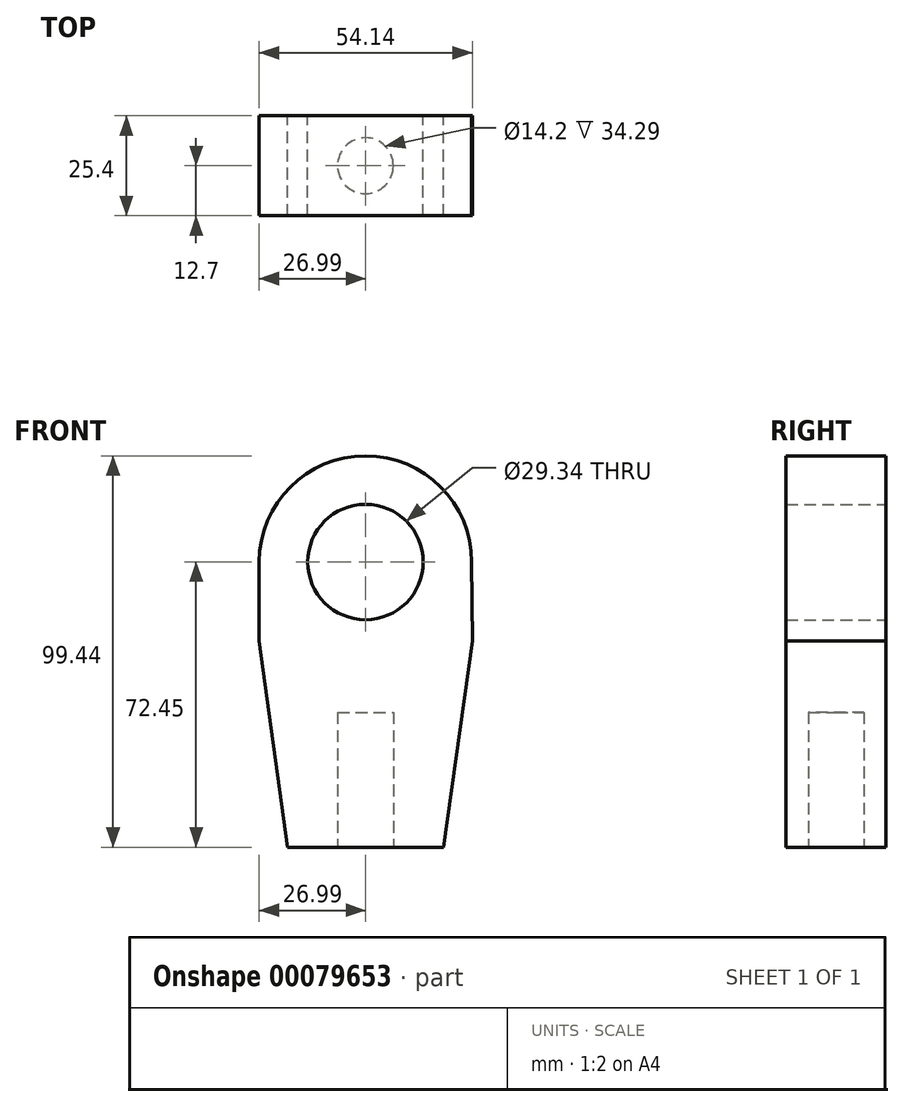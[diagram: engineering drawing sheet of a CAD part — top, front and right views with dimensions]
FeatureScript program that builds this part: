
annotation { "Feature Type Name" : "Feature", "Feature Type Description" : "" }
export const myFeature = defineFeature(function(context is Context, id is Id, definition is map)
    precondition{}
    {
        {
            var Q0;
            Q0=qCreatedBy(makeId("Front.planeOp"),FACE);
            var sketch = newSketch(context, id + "F0", { "sketchPlane" : qUnion([Q0])});
            skCircle(sketch, "E0", {"center": v(0, 0) * mm, "radius": 14.67 * mm});
            skCircle(sketch, "E1", {"center": v(0, 0) * mm, "radius": 26.99 * mm, "construction": true});
            skLineSegment(sketch, "E2", {"start": v(0, 26.99) * mm, "end": v(0, -72.45) * mm, "construction": true});
            skLineSegment(sketch, "E3", {"start": v(0, -72.45) * mm, "end": v(-19.81, -72.45) * mm});
            skLineSegment(sketch, "E4", {"start": v(0, -72.45) * mm, "end": v(19.81, -72.45) * mm});
            skArc(sketch, "E5", {"start": v(26.99, 0) * mm, "mid": v(0, 26.99) * mm, "end": v(-26.99, 0) * mm});
            skLineSegment(sketch, "E6", {"start": v(0, 26.99) * mm, "end": v(0, -20) * mm, "construction": true});
            skLineSegment(sketch, "E7", {"start": v(0, -20) * mm, "end": v(-28.93, -20) * mm, "construction": true});
            skLineSegment(sketch, "E8", {"start": v(0, -20) * mm, "end": v(27.15, -20) * mm, "construction": true});
            skLineSegment(sketch, "E9", {"start": v(-26.99, 0) * mm, "end": v(-26.99, -20) * mm});
            skLineSegment(sketch, "E10", {"start": v(26.99, 0) * mm, "end": v(27.15, -20) * mm});
            skLineSegment(sketch, "E11", {"start": v(-26.99, -20) * mm, "end": v(-19.81, -72.45) * mm});
            skLineSegment(sketch, "E12", {"start": v(27.15, -20) * mm, "end": v(19.81, -72.45) * mm});
            skSolve(sketch);
        }
        {
            var Q0;
            Q0 = qSketchRegion(id + "F0", true);
            extrude(context, id + "F1", {"entities" : qUnion([Q0]), "depth" : 25.4 * mm});
        }
        {
            var Q0;
            Q0=makeQuery(id+"F1.opExtrude","SWEPT_FACE",FACE,{"disambiguationData":[OSD([sQuery(id+"F0.wireOp",EDGE,"E3"),sQuery(id+"F0.wireOp",EDGE,"E4")])]});
            var sketch = newSketch(context, id + "F2", { "sketchPlane" : qUnion([Q0])});
            skCircle(sketch, "E13", {"center": v(0, 12.7) * mm, "radius": 7.1 * mm});
            skSolve(sketch);
        }
        {
            var Q0;
            Q0=makeQuery(id+"F2.imprint","IMPRINT",FACE,{"disambiguationData":[TD([[makeQuery(id+"F2.imprint","IMPRINT",EDGE,{"derivedFrom":sQuery(id+"F2.wireOp",EDGE,"E13")}),1.0]])]});
            extrude(context, id + "F3", {"entities" : qUnion([Q0]), "operationType" : NewBodyOperationType.REMOVE, "oppositeDirection" : true, "depth" : 34.3 * mm});
        }
    });
